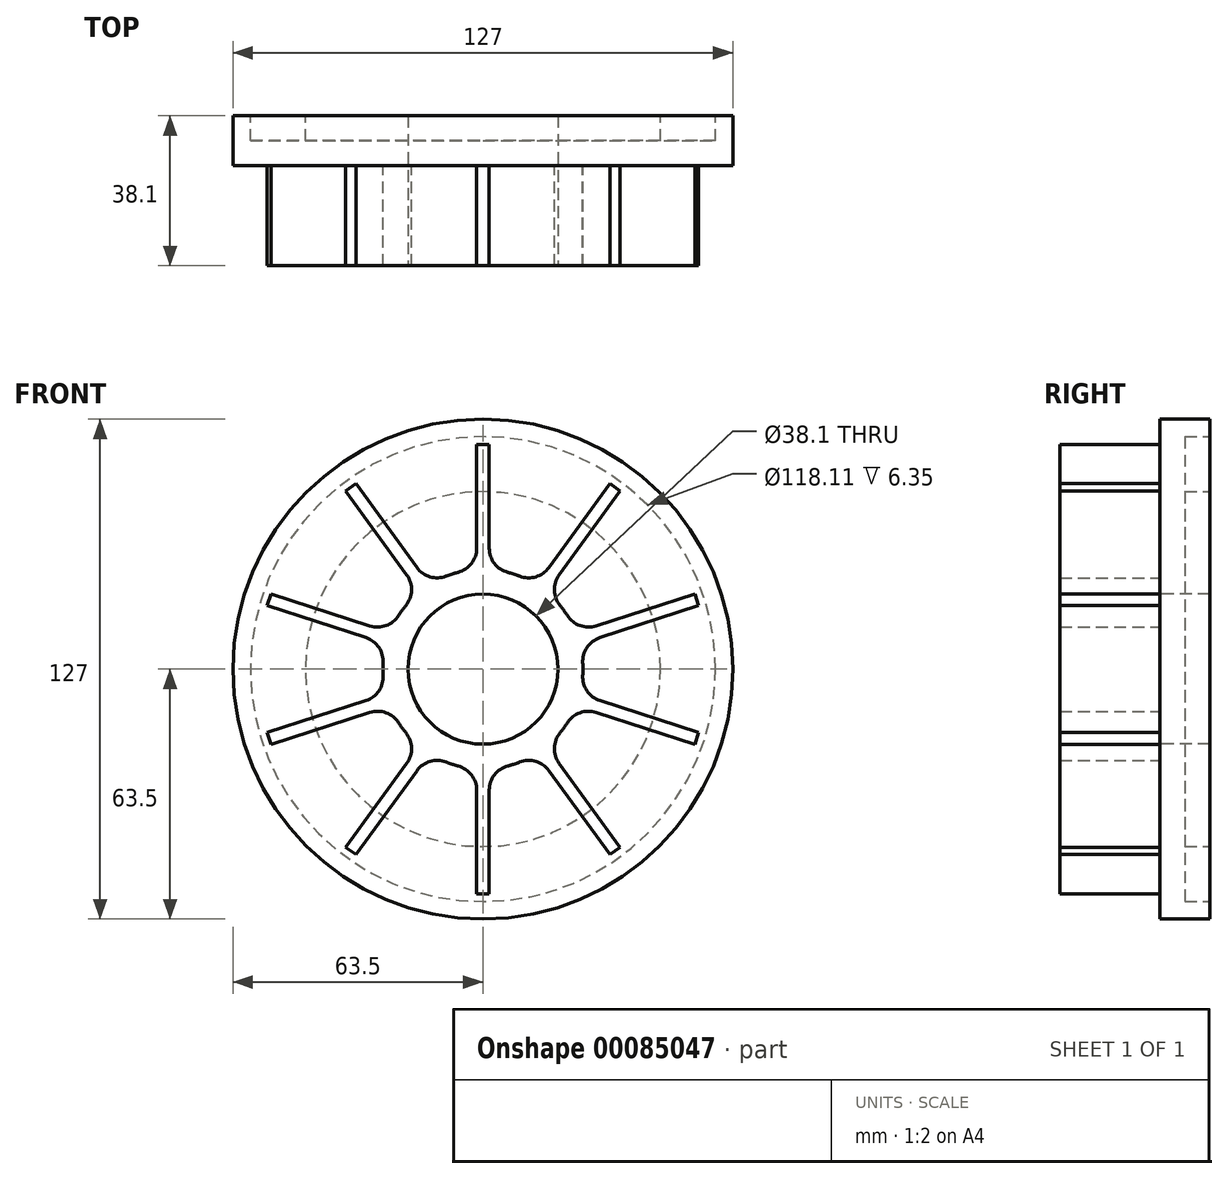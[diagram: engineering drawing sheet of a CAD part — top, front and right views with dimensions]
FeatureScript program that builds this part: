
annotation { "Feature Type Name" : "Feature", "Feature Type Description" : "" }
export const myFeature = defineFeature(function(context is Context, id is Id, definition is map)
    precondition{}
    {
        {
            var Q0;
            Q0=qCreatedBy(makeId("Front.planeOp"),FACE);
            var sketch = newSketch(context, id + "F0", { "sketchPlane" : qUnion([Q0])});
            skCircle(sketch, "E0", {"center": v(0, 0) * mm, "radius": 63.5 * mm});
            skSolve(sketch);
        }
        {
            var Q0;
            Q0 = qSketchRegion(id + "F0", true);
            extrude(context, id + "F1", {"entities" : qUnion([Q0]), "depth" : 12.7 * mm});
        }
        {
            var Q0;
            Q0=makeQuery(id+"F1.opExtrude","CAP_FACE",FACE,{"disambiguationData":[OSD([sQuery(id+"F0.wireOp",EDGE,"E0")])],"isStart":false});
            var sketch = newSketch(context, id + "F2", { "sketchPlane" : qUnion([Q0])});
            skPoint(sketch, "E1.0", {"position": v(0, 0) * mm});
            skCircle(sketch, "E2", {"center": v(0, 0) * mm, "radius": 25.4 * mm});
            skLineSegment(sketch, "E3", {"start": v(0, 0) * mm, "end": v(0, 117.5) * mm, "construction": true});
            skLineSegment(sketch, "E4", {"start": v(-1.59, 25.35) * mm, "end": v(-1.59, 57.1) * mm});
            skLineSegment(sketch, "E5", {"start": v(-1.59, 57.1) * mm, "end": v(0, 57.1) * mm});
            skLineSegment(sketch, "E6.MirrorCS", {"start": v(1.59, 57.1) * mm, "end": v(0, 57.1) * mm});
            skLineSegment(sketch, "E7.MirrorCS", {"start": v(1.59, 25.35) * mm, "end": v(1.59, 57.1) * mm});
            skLineSegment(sketch, "E8.1.0", {"start": v(-13.62, 21.44) * mm, "end": v(-32.28, 47.13) * mm});
            skLineSegment(sketch, "E8.1.1", {"start": v(-16.18, 19.58) * mm, "end": v(-34.85, 45.26) * mm});
            skLineSegment(sketch, "E8.1.2", {"start": v(-32.28, 47.13) * mm, "end": v(-33.56, 46.2) * mm});
            skLineSegment(sketch, "E8.1.3", {"start": v(-34.85, 45.26) * mm, "end": v(-33.56, 46.2) * mm});
            skLineSegment(sketch, "E8.2.0", {"start": v(-23.62, 9.34) * mm, "end": v(-53.82, 19.15) * mm});
            skLineSegment(sketch, "E8.2.1", {"start": v(-24.6, 6.32) * mm, "end": v(-54.8, 16.14) * mm});
            skLineSegment(sketch, "E8.2.2", {"start": v(-53.82, 19.15) * mm, "end": v(-54.3, 17.64) * mm});
            skLineSegment(sketch, "E8.2.3", {"start": v(-54.8, 16.14) * mm, "end": v(-54.3, 17.64) * mm});
            skLineSegment(sketch, "E9.1.3.0", {"start": v(-24.6, -6.32) * mm, "end": v(-54.8, -16.14) * mm});
            skLineSegment(sketch, "E9.3.3.0", {"start": v(-23.62, -9.34) * mm, "end": v(-53.82, -19.15) * mm});
            skLineSegment(sketch, "E9.6.3.0", {"start": v(-54.8, -16.14) * mm, "end": v(-54.3, -17.64) * mm});
            skLineSegment(sketch, "E9.9.3.0", {"start": v(-53.82, -19.15) * mm, "end": v(-54.3, -17.64) * mm});
            skLineSegment(sketch, "E9.1.4.0", {"start": v(-16.18, -19.58) * mm, "end": v(-34.85, -45.26) * mm});
            skLineSegment(sketch, "E9.3.4.0", {"start": v(-13.62, -21.44) * mm, "end": v(-32.28, -47.13) * mm});
            skLineSegment(sketch, "E9.6.4.0", {"start": v(-34.85, -45.26) * mm, "end": v(-33.56, -46.2) * mm});
            skLineSegment(sketch, "E9.9.4.0", {"start": v(-32.28, -47.13) * mm, "end": v(-33.56, -46.2) * mm});
            skLineSegment(sketch, "E9.1.5.0", {"start": v(-1.59, -25.35) * mm, "end": v(-1.59, -57.1) * mm});
            skLineSegment(sketch, "E9.3.5.0", {"start": v(1.59, -25.35) * mm, "end": v(1.59, -57.1) * mm});
            skLineSegment(sketch, "E9.6.5.0", {"start": v(-1.59, -57.1) * mm, "end": v(0, -57.1) * mm});
            skLineSegment(sketch, "E9.9.5.0", {"start": v(1.59, -57.1) * mm, "end": v(0, -57.1) * mm});
            skLineSegment(sketch, "E10.1.6.0", {"start": v(13.62, -21.44) * mm, "end": v(32.28, -47.13) * mm});
            skLineSegment(sketch, "E10.3.6.0", {"start": v(16.18, -19.58) * mm, "end": v(34.85, -45.26) * mm});
            skLineSegment(sketch, "E10.6.6.0", {"start": v(32.28, -47.13) * mm, "end": v(33.56, -46.2) * mm});
            skLineSegment(sketch, "E10.9.6.0", {"start": v(34.85, -45.26) * mm, "end": v(33.56, -46.2) * mm});
            skLineSegment(sketch, "E10.1.7.0", {"start": v(23.62, -9.34) * mm, "end": v(53.82, -19.15) * mm});
            skLineSegment(sketch, "E10.3.7.0", {"start": v(24.6, -6.32) * mm, "end": v(54.8, -16.14) * mm});
            skLineSegment(sketch, "E10.6.7.0", {"start": v(53.82, -19.15) * mm, "end": v(54.3, -17.64) * mm});
            skLineSegment(sketch, "E10.9.7.0", {"start": v(54.8, -16.14) * mm, "end": v(54.3, -17.64) * mm});
            skLineSegment(sketch, "E10.1.8.0", {"start": v(24.6, 6.32) * mm, "end": v(54.8, 16.14) * mm});
            skLineSegment(sketch, "E10.3.8.0", {"start": v(23.62, 9.34) * mm, "end": v(53.82, 19.15) * mm});
            skLineSegment(sketch, "E10.6.8.0", {"start": v(54.8, 16.14) * mm, "end": v(54.3, 17.64) * mm});
            skLineSegment(sketch, "E10.9.8.0", {"start": v(53.82, 19.15) * mm, "end": v(54.3, 17.64) * mm});
            skLineSegment(sketch, "E10.1.9.0", {"start": v(16.18, 19.58) * mm, "end": v(34.85, 45.26) * mm});
            skLineSegment(sketch, "E10.3.9.0", {"start": v(13.62, 21.44) * mm, "end": v(32.28, 47.13) * mm});
            skLineSegment(sketch, "E10.6.9.0", {"start": v(34.85, 45.26) * mm, "end": v(33.56, 46.2) * mm});
            skLineSegment(sketch, "E10.9.9.0", {"start": v(32.28, 47.13) * mm, "end": v(33.56, 46.2) * mm});
            skSolve(sketch);
        }
        {
            var Q0;
            Q0 = qSketchRegion(id + "F2", true);
            extrude(context, id + "F3", {"entities" : qUnion([Q0]), "operationType" : NewBodyOperationType.ADD, "depth" : 25.4 * mm});
        }
        {
            var Q0;
            Q0=makeQuery(id+"F3.opExtrude","SWEPT_EDGE",EDGE,{"disambiguationData":[OSD([sQuery(id+"F2.wireOp",EDGE,"E2"),sQuery(id+"F2.wireOp",EDGE,"E8.1.1")])]});
            var Q1;
            Q1=makeQuery(id+"F3.opExtrude","SWEPT_EDGE",EDGE,{"disambiguationData":[OSD([sQuery(id+"F2.wireOp",EDGE,"E2"),sQuery(id+"F2.wireOp",EDGE,"E4")])]});
            var Q2;
            Q2=makeQuery(id+"F3.opExtrude","SWEPT_EDGE",EDGE,{"disambiguationData":[OSD([sQuery(id+"F2.wireOp",EDGE,"E2"),sQuery(id+"F2.wireOp",EDGE,"E8.2.1")])]});
            var Q3;
            Q3=makeQuery(id+"F3.opExtrude","SWEPT_EDGE",EDGE,{"disambiguationData":[OSD([sQuery(id+"F2.wireOp",EDGE,"E2"),sQuery(id+"F2.wireOp",EDGE,"E9.1.3.0")])]});
            var Q4;
            Q4=makeQuery(id+"F3.opExtrude","SWEPT_EDGE",EDGE,{"disambiguationData":[OSD([sQuery(id+"F2.wireOp",EDGE,"E2"),sQuery(id+"F2.wireOp",EDGE,"E9.3.3.0")])]});
            var Q5;
            Q5=makeQuery(id+"F3.opExtrude","SWEPT_EDGE",EDGE,{"disambiguationData":[OSD([sQuery(id+"F2.wireOp",EDGE,"E2"),sQuery(id+"F2.wireOp",EDGE,"E9.1.4.0")])]});
            var Q6;
            Q6=makeQuery(id+"F3.opExtrude","SWEPT_EDGE",EDGE,{"disambiguationData":[OSD([sQuery(id+"F2.wireOp",EDGE,"E2"),sQuery(id+"F2.wireOp",EDGE,"E9.3.4.0")])]});
            var Q7;
            Q7=makeQuery(id+"F3.opExtrude","SWEPT_EDGE",EDGE,{"disambiguationData":[OSD([sQuery(id+"F2.wireOp",EDGE,"E2"),sQuery(id+"F2.wireOp",EDGE,"E9.1.5.0")])]});
            var Q8;
            Q8=makeQuery(id+"F3.opExtrude","SWEPT_EDGE",EDGE,{"disambiguationData":[OSD([sQuery(id+"F2.wireOp",EDGE,"E2"),sQuery(id+"F2.wireOp",EDGE,"E10.1.6.0")])]});
            var Q9;
            Q9=makeQuery(id+"F3.opExtrude","SWEPT_EDGE",EDGE,{"disambiguationData":[OSD([sQuery(id+"F2.wireOp",EDGE,"E2"),sQuery(id+"F2.wireOp",EDGE,"E9.3.5.0")])]});
            var Q10;
            Q10=makeQuery(id+"F3.opExtrude","SWEPT_EDGE",EDGE,{"disambiguationData":[OSD([sQuery(id+"F2.wireOp",EDGE,"E2"),sQuery(id+"F2.wireOp",EDGE,"E10.3.6.0")])]});
            var Q11;
            Q11=makeQuery(id+"F3.opExtrude","SWEPT_EDGE",EDGE,{"disambiguationData":[OSD([sQuery(id+"F2.wireOp",EDGE,"E2"),sQuery(id+"F2.wireOp",EDGE,"E10.1.7.0")])]});
            var Q12;
            Q12=makeQuery(id+"F3.opExtrude","SWEPT_EDGE",EDGE,{"disambiguationData":[OSD([sQuery(id+"F2.wireOp",EDGE,"E2"),sQuery(id+"F2.wireOp",EDGE,"E10.3.7.0")])]});
            var Q13;
            Q13=makeQuery(id+"F3.opExtrude","SWEPT_EDGE",EDGE,{"disambiguationData":[OSD([sQuery(id+"F2.wireOp",EDGE,"E2"),sQuery(id+"F2.wireOp",EDGE,"E10.1.8.0")])]});
            var Q14;
            Q14=makeQuery(id+"F3.opExtrude","SWEPT_EDGE",EDGE,{"disambiguationData":[OSD([sQuery(id+"F2.wireOp",EDGE,"E2"),sQuery(id+"F2.wireOp",EDGE,"E10.3.8.0")])]});
            var Q15;
            Q15=makeQuery(id+"F3.opExtrude","SWEPT_EDGE",EDGE,{"disambiguationData":[OSD([sQuery(id+"F2.wireOp",EDGE,"E2"),sQuery(id+"F2.wireOp",EDGE,"E10.1.9.0")])]});
            var Q16;
            Q16=makeQuery(id+"F3.opExtrude","SWEPT_EDGE",EDGE,{"disambiguationData":[OSD([sQuery(id+"F2.wireOp",EDGE,"E2"),sQuery(id+"F2.wireOp",EDGE,"E10.3.9.0")])]});
            var Q17;
            Q17=makeQuery(id+"F3.opExtrude","SWEPT_EDGE",EDGE,{"disambiguationData":[OSD([sQuery(id+"F2.wireOp",EDGE,"E2"),sQuery(id+"F2.wireOp",EDGE,"E7.MirrorCS")])]});
            var Q18;
            Q18=makeQuery(id+"F3.opExtrude","SWEPT_EDGE",EDGE,{"disambiguationData":[OSD([sQuery(id+"F2.wireOp",EDGE,"E2"),sQuery(id+"F2.wireOp",EDGE,"E8.1.0")])]});
            var Q19;
            Q19=makeQuery(id+"F3.opExtrude","SWEPT_EDGE",EDGE,{"disambiguationData":[OSD([sQuery(id+"F2.wireOp",EDGE,"E2"),sQuery(id+"F2.wireOp",EDGE,"E8.2.0")])]});
            fillet(context, id + "F4", {"entities" : qUnion([Q0, Q1, Q2, Q3, Q4, Q5, Q6, Q7, Q8, Q9, Q10, Q11, Q12, Q13, Q14, Q15, Q16, Q17, Q18, Q19]), "radius" : 6.35 * mm, "tangentPropagation" : true, "allowEdgeOverflow" : false});
        }
        {
            var Q0;
            Q0=makeQuery(id+"F3.opExtrude","CAP_FACE",FACE,{"disambiguationData":[OSD([sQuery(id+"F2.wireOp",EDGE,"E2"),sQuery(id+"F2.wireOp",EDGE,"E4"),sQuery(id+"F2.wireOp",EDGE,"E5"),sQuery(id+"F2.wireOp",EDGE,"E6.MirrorCS"),sQuery(id+"F2.wireOp",EDGE,"E7.MirrorCS"),sQuery(id+"F2.wireOp",EDGE,"E8.1.0"),sQuery(id+"F2.wireOp",EDGE,"E8.1.1"),sQuery(id+"F2.wireOp",EDGE,"E8.1.2"),sQuery(id+"F2.wireOp",EDGE,"E8.1.3"),sQuery(id+"F2.wireOp",EDGE,"E8.2.0"),sQuery(id+"F2.wireOp",EDGE,"E8.2.1"),sQuery(id+"F2.wireOp",EDGE,"E8.2.2"),sQuery(id+"F2.wireOp",EDGE,"E8.2.3"),sQuery(id+"F2.wireOp",EDGE,"E9.1.3.0"),sQuery(id+"F2.wireOp",EDGE,"E9.3.3.0"),sQuery(id+"F2.wireOp",EDGE,"E9.6.3.0"),sQuery(id+"F2.wireOp",EDGE,"E9.9.3.0"),sQuery(id+"F2.wireOp",EDGE,"E9.1.4.0"),sQuery(id+"F2.wireOp",EDGE,"E9.3.4.0"),sQuery(id+"F2.wireOp",EDGE,"E9.6.4.0"),sQuery(id+"F2.wireOp",EDGE,"E9.9.4.0"),sQuery(id+"F2.wireOp",EDGE,"E9.1.5.0"),sQuery(id+"F2.wireOp",EDGE,"E9.3.5.0"),sQuery(id+"F2.wireOp",EDGE,"E9.6.5.0"),sQuery(id+"F2.wireOp",EDGE,"E9.9.5.0"),sQuery(id+"F2.wireOp",EDGE,"E10.1.6.0"),sQuery(id+"F2.wireOp",EDGE,"E10.3.6.0"),sQuery(id+"F2.wireOp",EDGE,"E10.6.6.0"),sQuery(id+"F2.wireOp",EDGE,"E10.9.6.0"),sQuery(id+"F2.wireOp",EDGE,"E10.1.7.0"),sQuery(id+"F2.wireOp",EDGE,"E10.3.7.0"),sQuery(id+"F2.wireOp",EDGE,"E10.6.7.0"),sQuery(id+"F2.wireOp",EDGE,"E10.9.7.0"),sQuery(id+"F2.wireOp",EDGE,"E10.1.8.0"),sQuery(id+"F2.wireOp",EDGE,"E10.3.8.0"),sQuery(id+"F2.wireOp",EDGE,"E10.6.8.0"),sQuery(id+"F2.wireOp",EDGE,"E10.9.8.0"),sQuery(id+"F2.wireOp",EDGE,"E10.1.9.0"),sQuery(id+"F2.wireOp",EDGE,"E10.3.9.0"),sQuery(id+"F2.wireOp",EDGE,"E10.6.9.0"),sQuery(id+"F2.wireOp",EDGE,"E10.9.9.0")])],"isStart":false});
            var sketch = newSketch(context, id + "F5", { "sketchPlane" : qUnion([Q0])});
            skPoint(sketch, "E11.0", {"position": v(0, 0) * mm});
            skCircle(sketch, "E12", {"center": v(0, 0) * mm, "radius": 19.05 * mm});
            skSolve(sketch);
        }
        {
            var Q0;
            Q0 = qSketchRegion(id + "F5", true);
            extrude(context, id + "F6", {"entities" : qUnion([Q0]), "operationType" : NewBodyOperationType.REMOVE, "endBound" : BoundingType.THROUGH_ALL, "oppositeDirection" : true, "depth" : 25.4 * mm});
        }
        {
            var Q0;
            Q0=makeQuery(id+"F1.opExtrude","CAP_FACE",FACE,{"disambiguationData":[OSD([sQuery(id+"F0.wireOp",EDGE,"E0")])],"isStart":true});
            var sketch = newSketch(context, id + "F7", { "sketchPlane" : qUnion([Q0])});
            skPoint(sketch, "E13.0", {"position": v(0, 0) * mm});
            skCircle(sketch, "E14", {"center": v(0, 0) * mm, "radius": 59.06 * mm});
            skCircle(sketch, "E15", {"center": v(0, 0) * mm, "radius": 45.09 * mm});
            skSolve(sketch);
        }
        {
            var Q0;
            Q0 = qSketchRegion(id + "F7", true);
            extrude(context, id + "F8", {"entities" : qUnion([Q0]), "operationType" : NewBodyOperationType.REMOVE, "oppositeDirection" : true, "depth" : 6.35 * mm});
        }
    });
